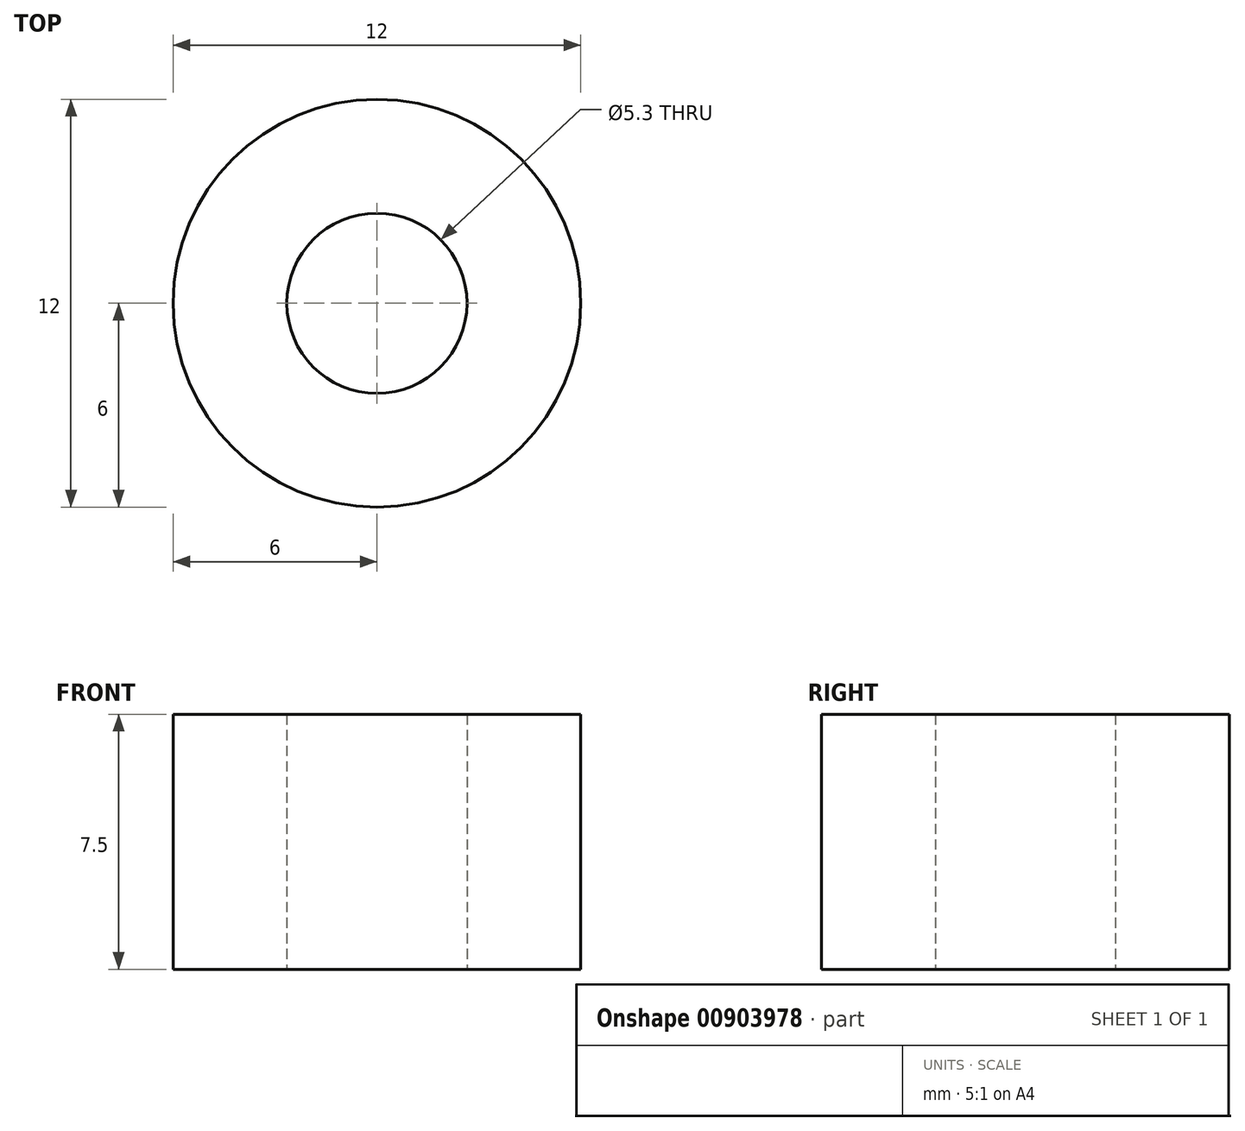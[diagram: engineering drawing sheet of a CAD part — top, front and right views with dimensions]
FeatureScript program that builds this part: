
annotation { "Feature Type Name" : "Feature", "Feature Type Description" : "" }
export const myFeature = defineFeature(function(context is Context, id is Id, definition is map)
    precondition{}
    {
        {
            var Q0;
            Q0=qCreatedBy(makeId("Top.planeOp"),FACE);
            var sketch = newSketch(context, id + "F0", { "sketchPlane" : qUnion([Q0])});
            skCircle(sketch, "E0", {"center": v(0, 0) * mm, "radius": 6 * mm});
            skCircle(sketch, "E1", {"center": v(0, 0) * mm, "radius": 2.65 * mm});
            skSolve(sketch);
        }
        {
            var Q0;
            Q0 = qSketchRegion(id + "F0", true);
            extrude(context, id + "F1", {"entities" : qUnion([Q0]), "depth" : 7.5 * mm, "offsetDistance" : 25 * mm});
        }
    });
